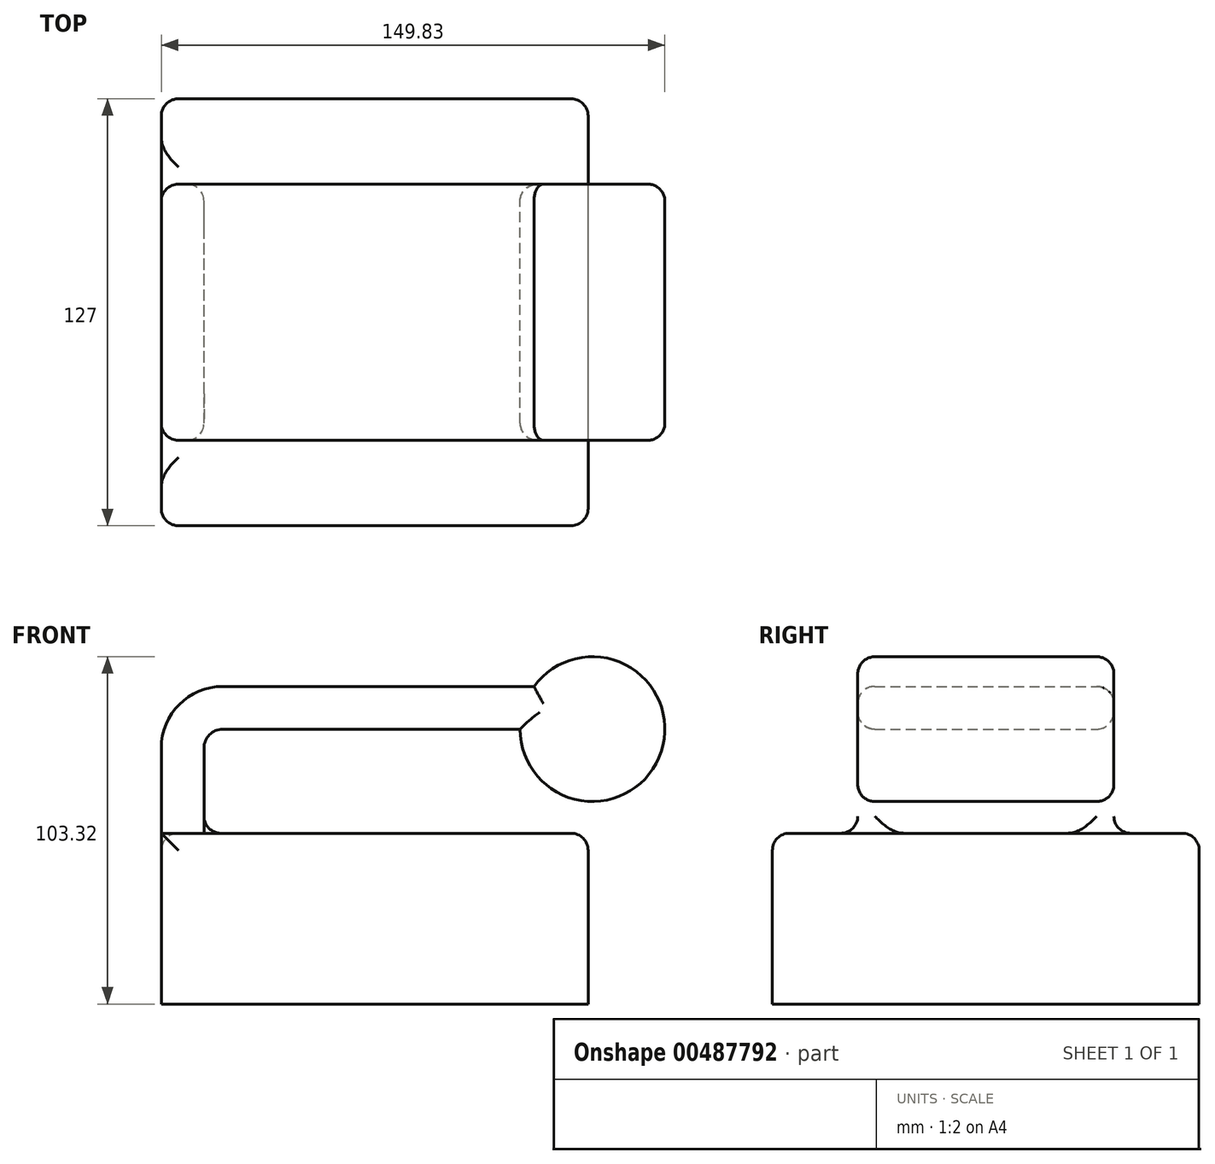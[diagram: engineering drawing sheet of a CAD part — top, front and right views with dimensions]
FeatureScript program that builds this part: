
annotation { "Feature Type Name" : "Feature", "Feature Type Description" : "" }
export const myFeature = defineFeature(function(context is Context, id is Id, definition is map)
    precondition{}
    {
        {
            var Q0;
            Q0=qCreatedBy(makeId("Front.planeOp"),FACE);
            var sketch = newSketch(context, id + "F0", { "sketchPlane" : qUnion([Q0])});
            skLineSegment(sketch, "E0.bottom", {"start": v(-63.5, -25.4) * mm, "end": v(63.5, -25.4) * mm});
            skLineSegment(sketch, "E0.top", {"start": v(-63.5, 25.4) * mm, "end": v(63.5, 25.4) * mm});
            skLineSegment(sketch, "E0.left", {"start": v(-63.5, -25.4) * mm, "end": v(-63.5, 25.4) * mm});
            skLineSegment(sketch, "E0.right", {"start": v(63.5, -25.4) * mm, "end": v(63.5, 25.4) * mm});
            skPoint(sketch, "E0.middle", {"position": v(0, 0) * mm});
            skCircle(sketch, "E1", {"center": v(64.79, 56.38) * mm, "radius": 21.54 * mm});
            skLineSegment(sketch, "E2", {"start": v(-63.5, 25.4) * mm, "end": v(-63.5, 50.8) * mm});
            skArc(sketch, "E3", {"start": v(-63.5, 50.8) * mm, "mid": v(-58.15, 63.73) * mm, "end": v(-45.22, 69.08) * mm});
            skLineSegment(sketch, "E4", {"start": v(-45.22, 69.08) * mm, "end": v(64.79, 69.08) * mm});
            skLineSegment(sketch, "E5.0", {"start": v(-45.22, 56.38) * mm, "end": v(64.79, 56.38) * mm});
            skArc(sketch, "E5.1", {"start": v(-50.8, 50.8) * mm, "mid": v(-49.17, 54.75) * mm, "end": v(-45.22, 56.38) * mm});
            skLineSegment(sketch, "E5.2", {"start": v(-50.8, 25.4) * mm, "end": v(-50.8, 50.8) * mm});
            skLineSegment(sketch, "E6", {"start": v(64.79, 69.08) * mm, "end": v(64.79, 56.38) * mm});
            skSolve(sketch);
        }
        {
            var Q0;
            Q0=makeQuery(id+"F0.imprint","IMPRINT",FACE,{"disambiguationData":[TD([[makeQuery(id+"F0.imprint","IMPRINT",EDGE,{"derivedFrom":sQuery(id+"F0.wireOp",EDGE,"E0.bottom")}),1.0]])]});
            extrude(context, id + "F1", {"entities" : qUnion([Q0]), "endBound" : BoundingType.SYMMETRIC, "depth" : 127 * mm});
        }
        {
            var Q0;
            {var subQ1=sQuery(id+"F0.wireOp",EDGE,"E2");Q0=makeQuery(id+"F0.imprint","IMPRINT",FACE,{"disambiguationData":[TD([[makeQuery(id+"F0.imprint","IMPRINT",EDGE,{"derivedFrom":subQ1}),-1.0]])]});}
            var Q1;
            {var subQ5=sQuery(id+"F0.wireOp",EDGE,"E6");Q1=makeQuery(id+"F0.imprint","IMPRINT",FACE,{"disambiguationData":[TD([[makeQuery(id+"F0.imprint","IMPRINT",EDGE,{"derivedFrom":subQ5}),-1.0]])]});}
            var Q2;
            {var subQ5=sQuery(id+"F0.wireOp",EDGE,"E6");Q2=makeQuery(id+"F0.imprint","IMPRINT",FACE,{"disambiguationData":[TD([[makeQuery(id+"F0.imprint","IMPRINT",EDGE,{"derivedFrom":subQ5}),1.0]])]});}
            extrude(context, id + "F2", {"entities" : qUnion([Q0, Q1, Q2]), "operationType" : NewBodyOperationType.ADD, "endBound" : BoundingType.SYMMETRIC, "depth" : 76.2 * mm});
        }
        {
            var Q0;
            Q0=makeQuery(id+"F1.opExtrude","CAP_EDGE",EDGE,{"disambiguationData":[OSD([sQuery(id+"F0.wireOp",EDGE,"E0.right")])],"isStart":false});
            var Q1;
            Q1=makeQuery(id+"F1.opExtrude","CAP_EDGE",EDGE,{"disambiguationData":[OSD([sQuery(id+"F0.wireOp",EDGE,"E0.left")])],"isStart":false});
            var Q2;
            Q2=makeQuery(id+"F1.opExtrude","CAP_EDGE",EDGE,{"disambiguationData":[OSD([sQuery(id+"F0.wireOp",EDGE,"E0.right")])],"isStart":true});
            var Q3;
            Q3=makeQuery(id+"F1.opExtrude","CAP_EDGE",EDGE,{"disambiguationData":[OSD([sQuery(id+"F0.wireOp",EDGE,"E0.left")])],"isStart":true});
            var Q4;
            Q4=makeQuery(id+"F2.opExtrude","CAP_FACE",FACE,{"disambiguationData":[OSD([sQuery(id+"F0.wireOp",EDGE,"E0.top"),sQuery(id+"F0.wireOp",EDGE,"E1"),sQuery(id+"F0.wireOp",EDGE,"E2"),sQuery(id+"F0.wireOp",EDGE,"E3"),sQuery(id+"F0.wireOp",EDGE,"E4"),sQuery(id+"F0.wireOp",EDGE,"E5.0"),sQuery(id+"F0.wireOp",EDGE,"E5.1"),sQuery(id+"F0.wireOp",EDGE,"E5.2")])],"isStart":false});
            var Q5;
            Q5=makeQuery(id+"F2.opExtrude","CAP_FACE",FACE,{"disambiguationData":[OSD([sQuery(id+"F0.wireOp",EDGE,"E0.top"),sQuery(id+"F0.wireOp",EDGE,"E1"),sQuery(id+"F0.wireOp",EDGE,"E2"),sQuery(id+"F0.wireOp",EDGE,"E3"),sQuery(id+"F0.wireOp",EDGE,"E4"),sQuery(id+"F0.wireOp",EDGE,"E5.0"),sQuery(id+"F0.wireOp",EDGE,"E5.1"),sQuery(id+"F0.wireOp",EDGE,"E5.2")])],"isStart":true});
            var Q6;
            Q6=makeQuery(id+"F1.opExtrude","CAP_EDGE",EDGE,{"disambiguationData":[OSD([sQuery(id+"F0.wireOp",EDGE,"E0.top")])],"isStart":false});
            var Q7;
            Q7=makeQuery(id+"F1.opExtrude","SWEPT_EDGE",EDGE,{"disambiguationData":[OSD([sQuery(id+"F0.wireOp",EDGE,"E0.top"),sQuery(id+"F0.wireOp",EDGE,"E0.right")])]});
            var Q8;
            Q8=makeQuery(id+"F1.opExtrude","CAP_EDGE",EDGE,{"disambiguationData":[OSD([sQuery(id+"F0.wireOp",EDGE,"E0.top")])],"isStart":true});
            fillet(context, id + "F3", {"entities" : qUnion([Q0, Q1, Q2, Q3, Q4, Q5, Q6, Q7, Q8]), "radius" : 5.08 * mm, "tangentPropagation" : true, "allowEdgeOverflow" : false});
        }
    });
